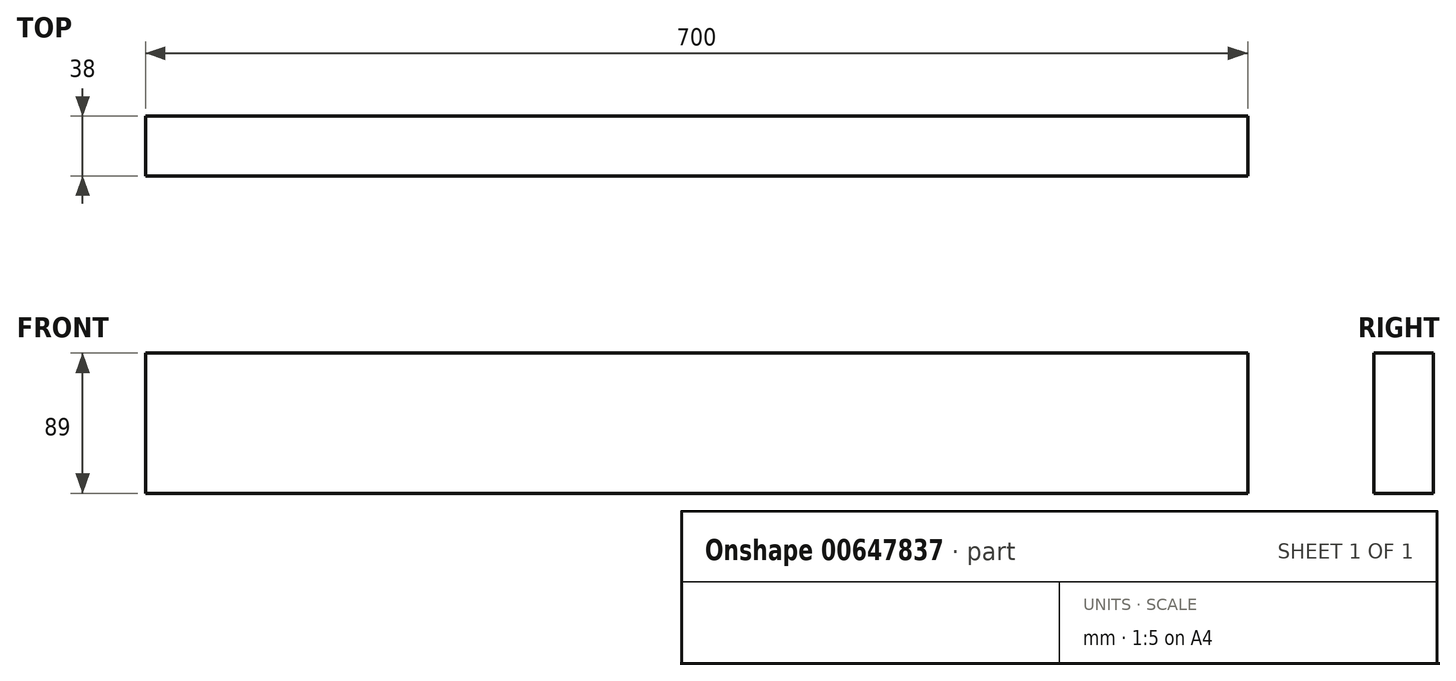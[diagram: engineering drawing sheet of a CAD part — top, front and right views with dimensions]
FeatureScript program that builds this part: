
annotation { "Feature Type Name" : "Feature", "Feature Type Description" : "" }
export const myFeature = defineFeature(function(context is Context, id is Id, definition is map)
    precondition{}
    {
        {
            var Q0;
            Q0=qCreatedBy(makeId("Front.planeOp"),FACE);
            var sketch = newSketch(context, id + "F0", { "sketchPlane" : qUnion([Q0])});
            skLineSegment(sketch, "E0.bottom", {"start": v(-350, -44.5) * mm, "end": v(350, -44.5) * mm});
            skLineSegment(sketch, "E0.top", {"start": v(-350, 44.5) * mm, "end": v(350, 44.5) * mm});
            skLineSegment(sketch, "E0.left", {"start": v(-350, -44.5) * mm, "end": v(-350, 44.5) * mm});
            skLineSegment(sketch, "E0.right", {"start": v(350, -44.5) * mm, "end": v(350, 44.5) * mm});
            skPoint(sketch, "E0.middle", {"position": v(0, 0) * mm});
            skSolve(sketch);
        }
        {
            var Q0;
            Q0 = qSketchRegion(id + "F0", true);
            extrude(context, id + "F1", {"entities" : qUnion([Q0]), "depth" : 38 * mm, "offsetDistance" : 25 * mm});
        }
    });
